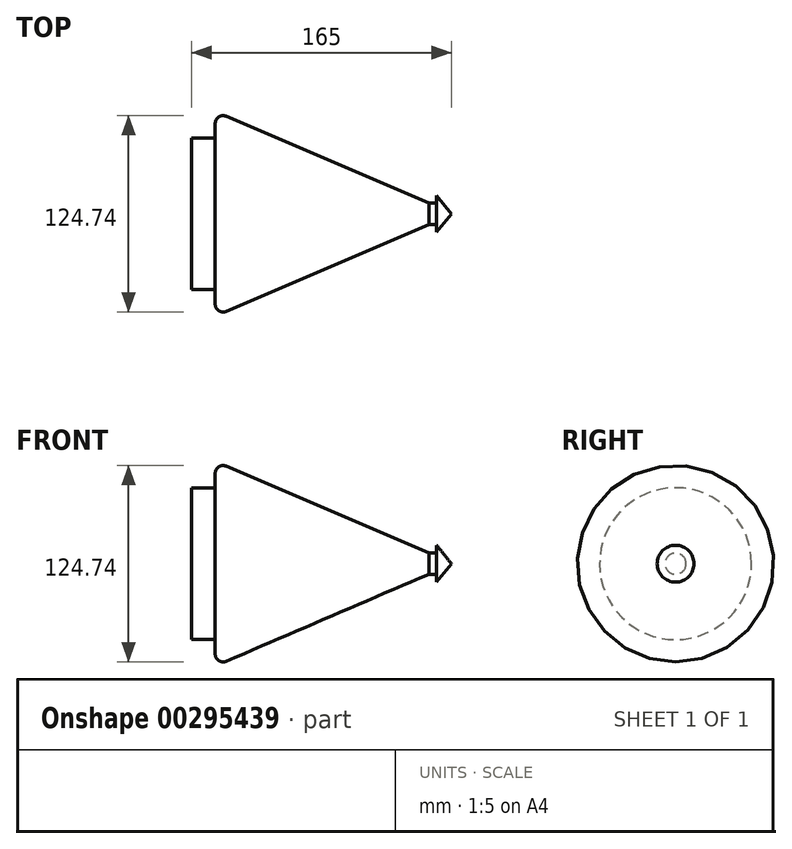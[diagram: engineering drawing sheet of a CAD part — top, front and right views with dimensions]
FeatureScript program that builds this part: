
annotation { "Feature Type Name" : "Feature", "Feature Type Description" : "" }
export const myFeature = defineFeature(function(context is Context, id is Id, definition is map)
    precondition{}
    {
        {
            var Q0;
            Q0=qCreatedBy(makeId("Top.planeOp"),FACE);
            var sketch = newSketch(context, id + "F0", { "sketchPlane" : qUnion([Q0])});
            skLineSegment(sketch, "E0", {"start": v(0, 0) * mm, "end": v(216.94, 0) * mm, "construction": true});
            skLineSegment(sketch, "E1", {"start": v(0, 0) * mm, "end": v(-213.83, 0) * mm, "construction": true});
            skLineSegment(sketch, "E2", {"start": v(0, 0) * mm, "end": v(0, 48.23) * mm});
            skLineSegment(sketch, "E3", {"start": v(0, 48.23) * mm, "end": v(15, 48.23) * mm});
            skLineSegment(sketch, "E4", {"start": v(15, 48.23) * mm, "end": v(15, 57.37) * mm});
            skPoint(sketch, "E5.visualSharp", {"position": v(15, 63.23) * mm});
            skArc(sketch, "E5.filletArc", {"start": v(21.97, 61.96) * mm, "mid": v(17.25, 61.54) * mm, "end": v(15, 57.37) * mm});
            skLineSegment(sketch, "E6", {"start": v(21.97, 61.96) * mm, "end": v(150.61, 6.7) * mm});
            skLineSegment(sketch, "E7", {"start": v(150.61, 6.7) * mm, "end": v(155.61, 6.7) * mm});
            skLineSegment(sketch, "E8", {"start": v(155.61, 6.7) * mm, "end": v(155.61, 11.7) * mm});
            skLineSegment(sketch, "E9", {"start": v(155.61, 11.7) * mm, "end": v(165, 0) * mm});
            skLineSegment(sketch, "E10", {"start": v(165, 0) * mm, "end": v(0, 0) * mm});
            skSolve(sketch);
        }
        {
            var Q0;
            Q0=makeQuery(id+"F0.imprint","IMPRINT",FACE,{"disambiguationData":[TD([[makeQuery(id+"F0.imprint","IMPRINT",EDGE,{"derivedFrom":sQuery(id+"F0.wireOp",EDGE,"E2")}),-1.0]])]});
            var Q1;
            Q1=sQuery(id+"F0.wireOp",EDGE,"E1");
            revolve(context, id + "F1", {"entities" : qUnion([Q0]), "axis" : qUnion([Q1]), "revolveType" : RevolveType.FULL});
        }
    });
